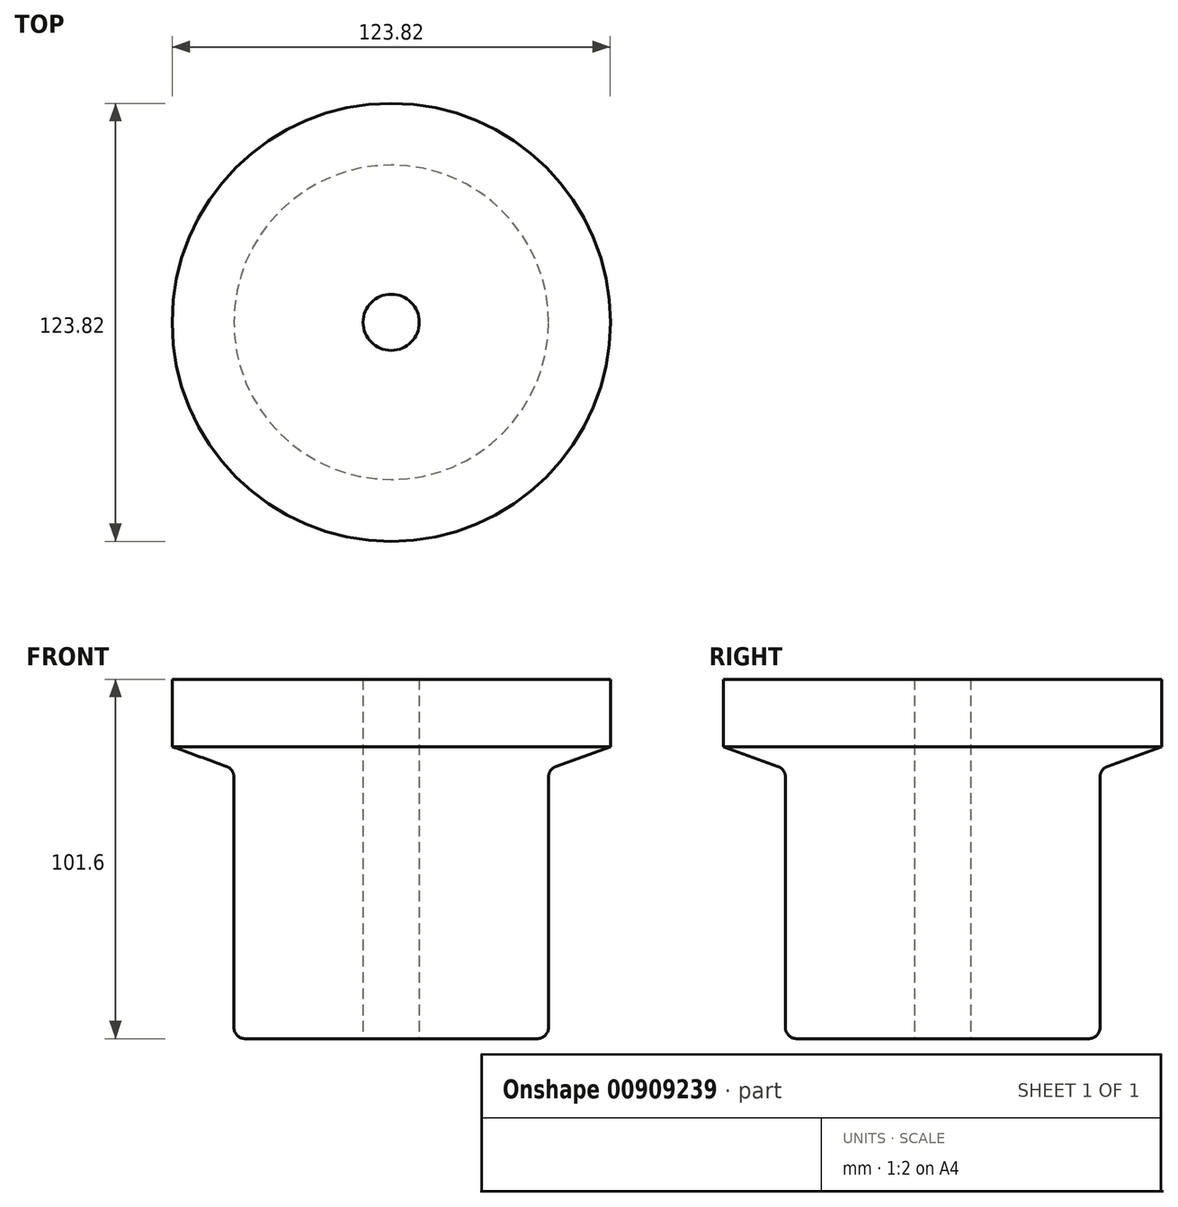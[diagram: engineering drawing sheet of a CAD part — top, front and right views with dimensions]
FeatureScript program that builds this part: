
annotation { "Feature Type Name" : "Feature", "Feature Type Description" : "" }
export const myFeature = defineFeature(function(context is Context, id is Id, definition is map)
    precondition{}
    {
        {
            var Q0;
            Q0=qCreatedBy(makeId("Front.planeOp"),FACE);
            var sketch = newSketch(context, id + "F0", { "sketchPlane" : qUnion([Q0])});
            skLineSegment(sketch, "E0", {"start": v(0, 0) * mm, "end": v(0, 88.35) * mm, "construction": true});
            skLineSegment(sketch, "E1", {"start": v(7.94, 0) * mm, "end": v(7.94, 101.6) * mm});
            skLineSegment(sketch, "E2", {"start": v(58.74, 101.6) * mm, "end": v(7.94, 101.6) * mm});
            skLineSegment(sketch, "E3", {"start": v(61.91, 98.42) * mm, "end": v(61.91, 82.55) * mm});
            skLineSegment(sketch, "E4", {"start": v(61.91, 82.55) * mm, "end": v(46.54, 76.96) * mm});
            skLineSegment(sketch, "E5", {"start": v(44.45, 73.98) * mm, "end": v(44.45, 3.18) * mm});
            skLineSegment(sketch, "E6", {"start": v(41.28, 0) * mm, "end": v(7.94, 0) * mm});
            skPoint(sketch, "E7.visualSharp", {"position": v(44.45, 76.2) * mm});
            skArc(sketch, "E7.filletArc", {"start": v(46.54, 76.96) * mm, "mid": v(45.02, 75.8) * mm, "end": v(44.45, 73.98) * mm});
            skPoint(sketch, "E8.visualSharp", {"position": v(61.91, 101.6) * mm});
            skPoint(sketch, "E9.visualSharp", {"position": v(44.45, 0) * mm});
            skArc(sketch, "E9.filletArc", {"start": v(41.28, 0) * mm, "mid": v(43.52, 0.93) * mm, "end": v(44.45, 3.18) * mm});
            skLineSegment(sketch, "E10", {"start": v(58.74, 101.6) * mm, "end": v(61.91, 101.6) * mm});
            skLineSegment(sketch, "E11", {"start": v(61.91, 98.42) * mm, "end": v(61.91, 101.6) * mm});
            skSolve(sketch);
        }
        {
            var Q0;
            Q0 = qSketchRegion(id + "F0", true);
            var Q1;
            Q1=sQuery(id+"F0.wireOp",EDGE,"E0");
            revolve(context, id + "F1", {"surfaceOperationType" : NewSurfaceOperationType.NEW, "entities" : qUnion([Q0]), "axis" : qUnion([Q1]), "revolveType" : RevolveType.FULL});
        }
    });
